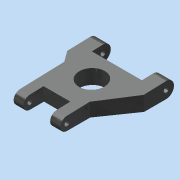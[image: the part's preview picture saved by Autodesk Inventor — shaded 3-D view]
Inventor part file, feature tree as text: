
AUTODESK INVENTOR PART (.ipt)
format: ipt  version: 2013 (Build 170138000, 138)  size: 131,584 bytes
history: native  units: in
note: dims shown in document units (in); Inventor stores cm internally (conversion verified against a paired STEP export)
features: other x3, sketch x2, plane x2
ambient origin geometry x8: Origin, YZ Plane, XZ Plane, XY Plane, X Axis, Y Axis, Z Axis, Center Point
bodies: Solid1 (feature_tree)
feature tree (7):
  other  "Shock Plate - Bottom (Right).ipt"
  other  "Solid1::Shock Plate - Bottom (Right).ipt"
  other  "TaggingFeature1"
  sketch  "Sketch2"  dims[d0=0.3937in]
  sketch  "Sketch3"  dims[d1=0.115in d2=0.37in d3=0.115in d4=2.16in d5=1.8in d6=0.0in d10=0.23in d12=0.63in d14=1.2in d16=0.31in d17=0.44in d18=0.48in d20=0.0in d21=1.45in d22=0.24in d24=0.7in d25=0.61in d26=0.24in d27=0.37in d28=1.18in d29=0.18in]
  plane  "Work Plane1"
  plane  "Work Plane2"
